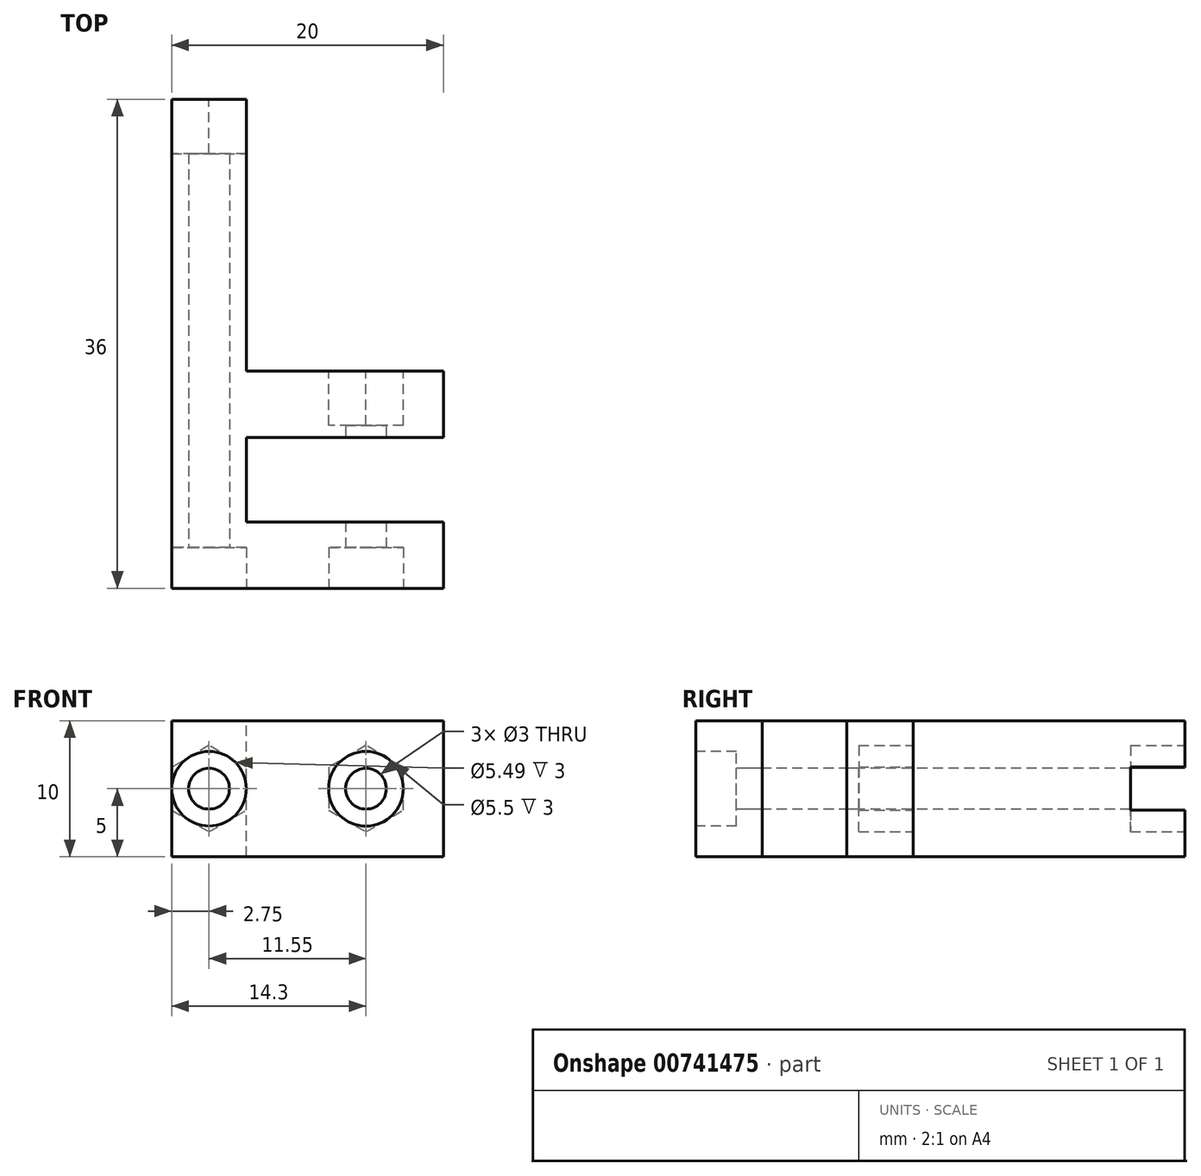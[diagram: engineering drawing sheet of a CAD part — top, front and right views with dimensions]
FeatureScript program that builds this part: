
annotation { "Feature Type Name" : "Feature", "Feature Type Description" : "" }
export const myFeature = defineFeature(function(context is Context, id is Id, definition is map)
    precondition{}
    {
        {
            var Q0;
            Q0=qCreatedBy(makeId("Top.planeOp"),FACE);
            var sketch = newSketch(context, id + "F0", { "sketchPlane" : qUnion([Q0])});
            skLineSegment(sketch, "E0", {"start": v(0, -8) * mm, "end": v(-20, -8) * mm});
            skLineSegment(sketch, "E1", {"start": v(-20, -8) * mm, "end": v(-20, 0) * mm});
            skLineSegment(sketch, "E2", {"start": v(0, -3.1) * mm, "end": v(0, -8) * mm});
            skLineSegment(sketch, "E3", {"start": v(-14.5, -3.1) * mm, "end": v(-14.5, 0) * mm});
            skLineSegment(sketch, "E4.MirrorCS", {"start": v(0, 8) * mm, "end": v(-20, 8) * mm});
            skLineSegment(sketch, "E5.MirrorCS", {"start": v(-20, 8) * mm, "end": v(-20, 0) * mm});
            skLineSegment(sketch, "E6.MirrorCS", {"start": v(-14.5, 3.1) * mm, "end": v(-14.5, 0) * mm});
            skLineSegment(sketch, "E7.MirrorCS", {"start": v(0, 3.1) * mm, "end": v(0, 8) * mm});
            skLineSegment(sketch, "E8.MirrorCS", {"start": v(0, 3.1) * mm, "end": v(-14.5, 3.1) * mm});
            skLineSegment(sketch, "E9", {"start": v(-14.5, -3.1) * mm, "end": v(0, -3.1) * mm});
            skSolve(sketch);
        }
        {
            var Q0;
            Q0=makeQuery(id+"F0.imprint","IMPRINT",FACE,{"disambiguationData":[TD([[makeQuery(id+"F0.imprint","IMPRINT",EDGE,{"derivedFrom":sQuery(id+"F0.wireOp",EDGE,"E0")}),-1.0]])]});
            extrude(context, id + "F1", {"entities" : qUnion([Q0]), "depth" : 10 * mm, "offsetDistance" : 25 * mm});
        }
        {
            var Q0;
            Q0=makeQuery(id+"F1.opExtrude","SWEPT_FACE",FACE,{"disambiguationData":[OSD([sQuery(id+"F0.wireOp",EDGE,"E0")])]});
            var sketch = newSketch(context, id + "F2", { "sketchPlane" : qUnion([Q0])});
            skCircle(sketch, "E10", {"center": v(-17.25, 5) * mm, "radius": 1.5 * mm});
            skCircle(sketch, "E11", {"center": v(-5.7, 5) * mm, "radius": 1.5 * mm});
            skCircle(sketch, "E12", {"center": v(-17.25, 5) * mm, "radius": 2.75 * mm});
            skCircle(sketch, "E13", {"center": v(-5.7, 5) * mm, "radius": 2.75 * mm});
            skSolve(sketch);
        }
        {
            var Q0;
            Q0=makeQuery(id+"F2.imprint","IMPRINT",FACE,{"disambiguationData":[TD([[makeQuery(id+"F2.imprint","IMPRINT",EDGE,{"derivedFrom":sQuery(id+"F2.wireOp",EDGE,"E10")}),1.0]])]});
            var Q1;
            Q1=makeQuery(id+"F2.imprint","IMPRINT",FACE,{"disambiguationData":[TD([[makeQuery(id+"F2.imprint","IMPRINT",EDGE,{"derivedFrom":sQuery(id+"F2.wireOp",EDGE,"E11")}),1.0]])]});
            extrude(context, id + "F3", {"entities" : qUnion([Q0, Q1]), "operationType" : NewBodyOperationType.REMOVE, "oppositeDirection" : true, "depth" : 16 * mm, "offsetDistance" : 25 * mm});
        }
        {
            var Q0;
            Q0=makeQuery(id+"F1.opExtrude","SWEPT_FACE",FACE,{"disambiguationData":[OSD([sQuery(id+"F0.wireOp",EDGE,"E4.MirrorCS")])]});
            var sketch = newSketch(context, id + "F4", { "sketchPlane" : qUnion([Q0])});
            skCircle(sketch, "E14.cCircle", {"center": v(5.7, 5) * mm, "radius": 2.75 * mm, "construction": true});
            skLineSegment(sketch, "E14.0", {"start": v(8.45, 6.59) * mm, "end": v(8.45, 3.41) * mm});
            skLineSegment(sketch, "E14.1", {"start": v(8.45, 3.41) * mm, "end": v(5.7, 1.82) * mm});
            skLineSegment(sketch, "E14.2", {"start": v(5.7, 1.82) * mm, "end": v(2.95, 3.41) * mm});
            skLineSegment(sketch, "E14.3", {"start": v(2.95, 3.41) * mm, "end": v(2.95, 6.59) * mm});
            skLineSegment(sketch, "E14.4", {"start": v(2.95, 6.59) * mm, "end": v(5.7, 8.18) * mm});
            skLineSegment(sketch, "E14.5", {"start": v(5.7, 8.18) * mm, "end": v(8.45, 6.59) * mm});
            skPoint(sketch, "E14.0.midPoint", {"position": v(8.45, 5) * mm});
            skPoint(sketch, "E15", {"position": v(17.25, 5) * mm});
            skLineSegment(sketch, "E16.bottom", {"start": v(20, 10) * mm, "end": v(14.5, 10) * mm});
            skLineSegment(sketch, "E16.top", {"start": v(20, 0) * mm, "end": v(14.5, 0) * mm});
            skLineSegment(sketch, "E16.left", {"start": v(20, 10) * mm, "end": v(20, 0) * mm});
            skLineSegment(sketch, "E16.right", {"start": v(14.5, 10) * mm, "end": v(14.5, 0) * mm});
            skSolve(sketch);
        }
        {
            var Q0;
            Q0=makeQuery(id+"F4.imprint","IMPRINT",FACE,{"disambiguationData":[TD([[makeQuery(id+"F4.imprint","IMPRINT",EDGE,{"derivedFrom":sQuery(id+"F4.wireOp",EDGE,"E14.0")}),-1.0]])]});
            extrude(context, id + "F5", {"entities" : qUnion([Q0]), "operationType" : NewBodyOperationType.REMOVE, "oppositeDirection" : true, "depth" : 4 * mm, "offsetDistance" : 25 * mm});
        }
        {
            var Q0;
            Q0=makeQuery(id+"F2.imprint","IMPRINT",FACE,{"disambiguationData":[TD([[makeQuery(id+"F2.imprint","IMPRINT",EDGE,{"derivedFrom":sQuery(id+"F2.wireOp",EDGE,"E10")}),-1.0]])]});
            var Q1;
            Q1=makeQuery(id+"F2.imprint","IMPRINT",FACE,{"disambiguationData":[TD([[makeQuery(id+"F2.imprint","IMPRINT",EDGE,{"derivedFrom":sQuery(id+"F2.wireOp",EDGE,"E11")}),-1.0]])]});
            extrude(context, id + "F6", {"entities" : qUnion([Q0, Q1]), "operationType" : NewBodyOperationType.REMOVE, "oppositeDirection" : true, "depth" : 3 * mm, "offsetDistance" : 25 * mm});
        }
        {
            var Q0;
            Q0=makeQuery(id+"F4.imprint","IMPRINT",FACE,{"disambiguationData":[TD([[makeQuery(id+"F4.imprint","IMPRINT",EDGE,{"derivedFrom":sQuery(id+"F4.wireOp",EDGE,"E16.bottom")}),-1.0]])]});
            extrude(context, id + "F7", {"entities" : qUnion([Q0]), "operationType" : NewBodyOperationType.ADD, "depth" : 20 * mm, "offsetDistance" : 25 * mm});
        }
        {
            var Q0;
            Q0=makeQuery(id+"F7.opExtrude","CAP_FACE",FACE,{"disambiguationData":[OSD([sQuery(id+"F2.wireOp",EDGE,"E10"),sQuery(id+"F4.wireOp",EDGE,"E16.bottom"),sQuery(id+"F4.wireOp",EDGE,"E16.top"),sQuery(id+"F4.wireOp",EDGE,"E16.left"),sQuery(id+"F4.wireOp",EDGE,"E16.right")])],"isStart":false});
            var sketch = newSketch(context, id + "F8", { "sketchPlane" : qUnion([Q0])});
            skCircle(sketch, "E17.cCircle", {"center": v(17.25, 5) * mm, "radius": 3.17 * mm, "construction": true});
            skLineSegment(sketch, "E17.0", {"start": v(20, 6.58) * mm, "end": v(20, 3.41) * mm});
            skLineSegment(sketch, "E17.1", {"start": v(20, 3.41) * mm, "end": v(17.25, 1.83) * mm});
            skLineSegment(sketch, "E17.2", {"start": v(17.25, 1.83) * mm, "end": v(14.5, 3.42) * mm});
            skLineSegment(sketch, "E17.3", {"start": v(14.5, 3.42) * mm, "end": v(14.5, 6.59) * mm});
            skLineSegment(sketch, "E17.4", {"start": v(14.5, 6.59) * mm, "end": v(17.25, 8.17) * mm});
            skLineSegment(sketch, "E17.5", {"start": v(17.25, 8.17) * mm, "end": v(20, 6.58) * mm});
            skSolve(sketch);
        }
        {
            var Q0;
            Q0=makeQuery(id+"F8.imprint","IMPRINT",FACE,{"disambiguationData":[TD([[makeQuery(id+"F8.imprint","IMPRINT",EDGE,{"derivedFrom":sQuery(id+"F8.wireOp",EDGE,"E17.0")}),-1.0]])]});
            extrude(context, id + "F9", {"entities" : qUnion([Q0]), "operationType" : NewBodyOperationType.REMOVE, "oppositeDirection" : true, "depth" : 4 * mm, "offsetDistance" : 25 * mm});
        }
    });
